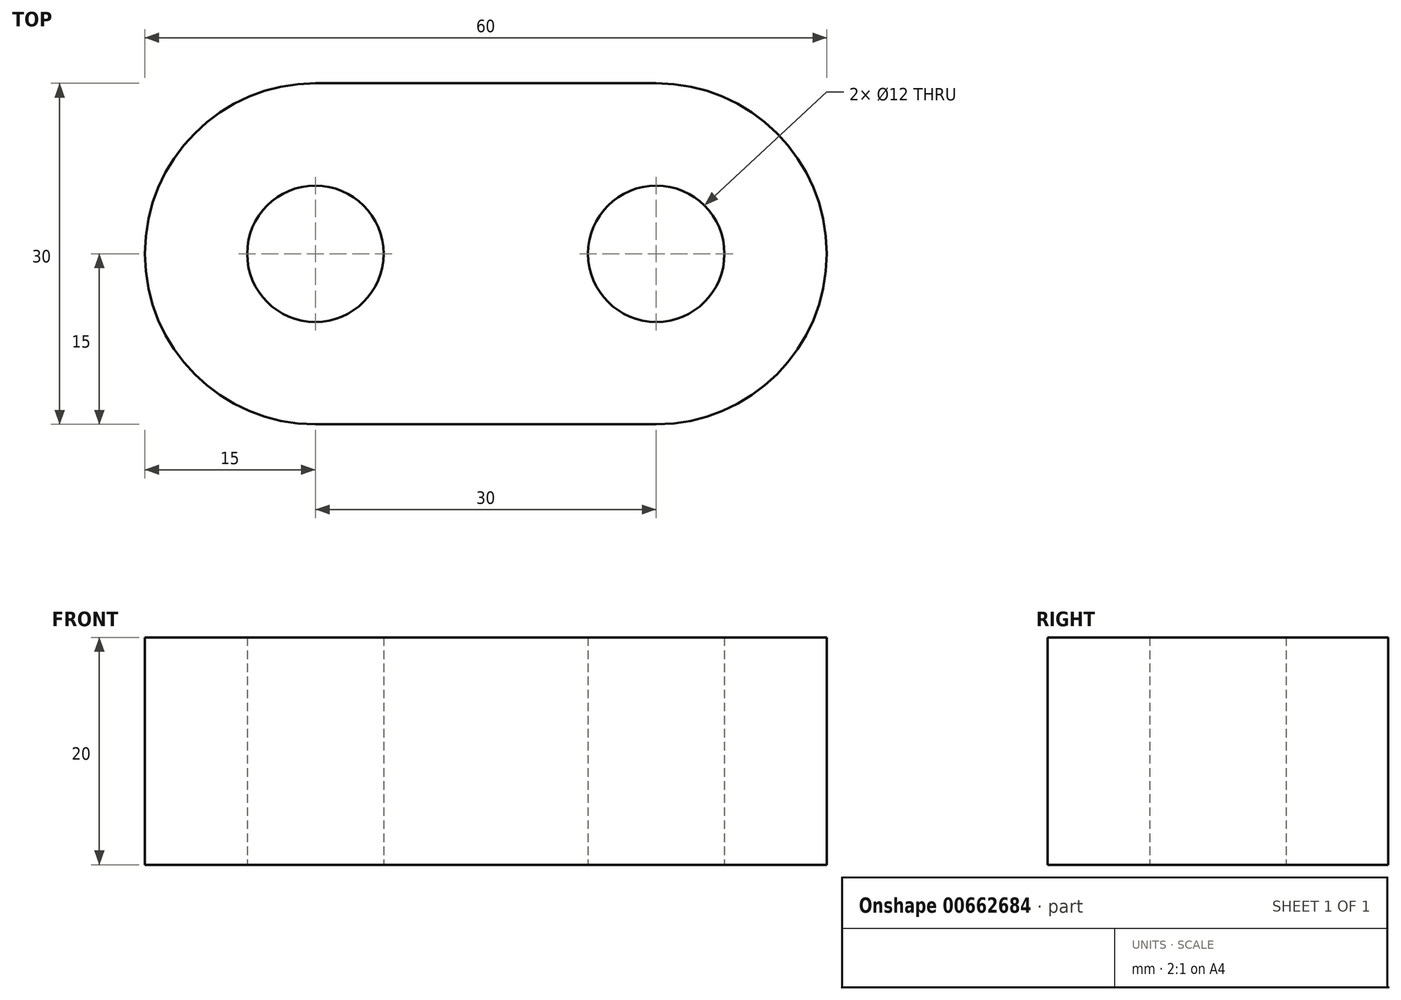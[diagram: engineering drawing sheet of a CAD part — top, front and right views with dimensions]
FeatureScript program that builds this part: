
annotation { "Feature Type Name" : "Feature", "Feature Type Description" : "" }
export const myFeature = defineFeature(function(context is Context, id is Id, definition is map)
    precondition{}
    {
        {
            var Q0;
            Q0=qCreatedBy(makeId("Top.planeOp"),FACE);
            var sketch = newSketch(context, id + "F0", { "sketchPlane" : qUnion([Q0])});
            skLineSegment(sketch, "E0", {"start": v(-15, 15) * mm, "end": v(15, 15) * mm});
            skLineSegment(sketch, "E1", {"start": v(-15, -15) * mm, "end": v(15, -15) * mm});
            skArc(sketch, "E2", {"start": v(15, -15) * mm, "mid": v(30, 0) * mm, "end": v(15, 15) * mm});
            skArc(sketch, "E3", {"start": v(-15, 15) * mm, "mid": v(-30, 0) * mm, "end": v(-15, -15) * mm});
            skCircle(sketch, "E4", {"center": v(-15, 0) * mm, "radius": 6 * mm});
            skCircle(sketch, "E5", {"center": v(15, 0) * mm, "radius": 6 * mm});
            skSolve(sketch);
        }
        {
            var Q0;
            Q0=makeQuery(id+"F0.imprint","IMPRINT",FACE,{"disambiguationData":[TD([[makeQuery(id+"F0.imprint","IMPRINT",EDGE,{"derivedFrom":sQuery(id+"F0.wireOp",EDGE,"E0")}),-1.0]])]});
            extrude(context, id + "F1", {"entities" : qUnion([Q0]), "depth" : 20 * mm, "offsetDistance" : 25 * mm});
        }
    });
